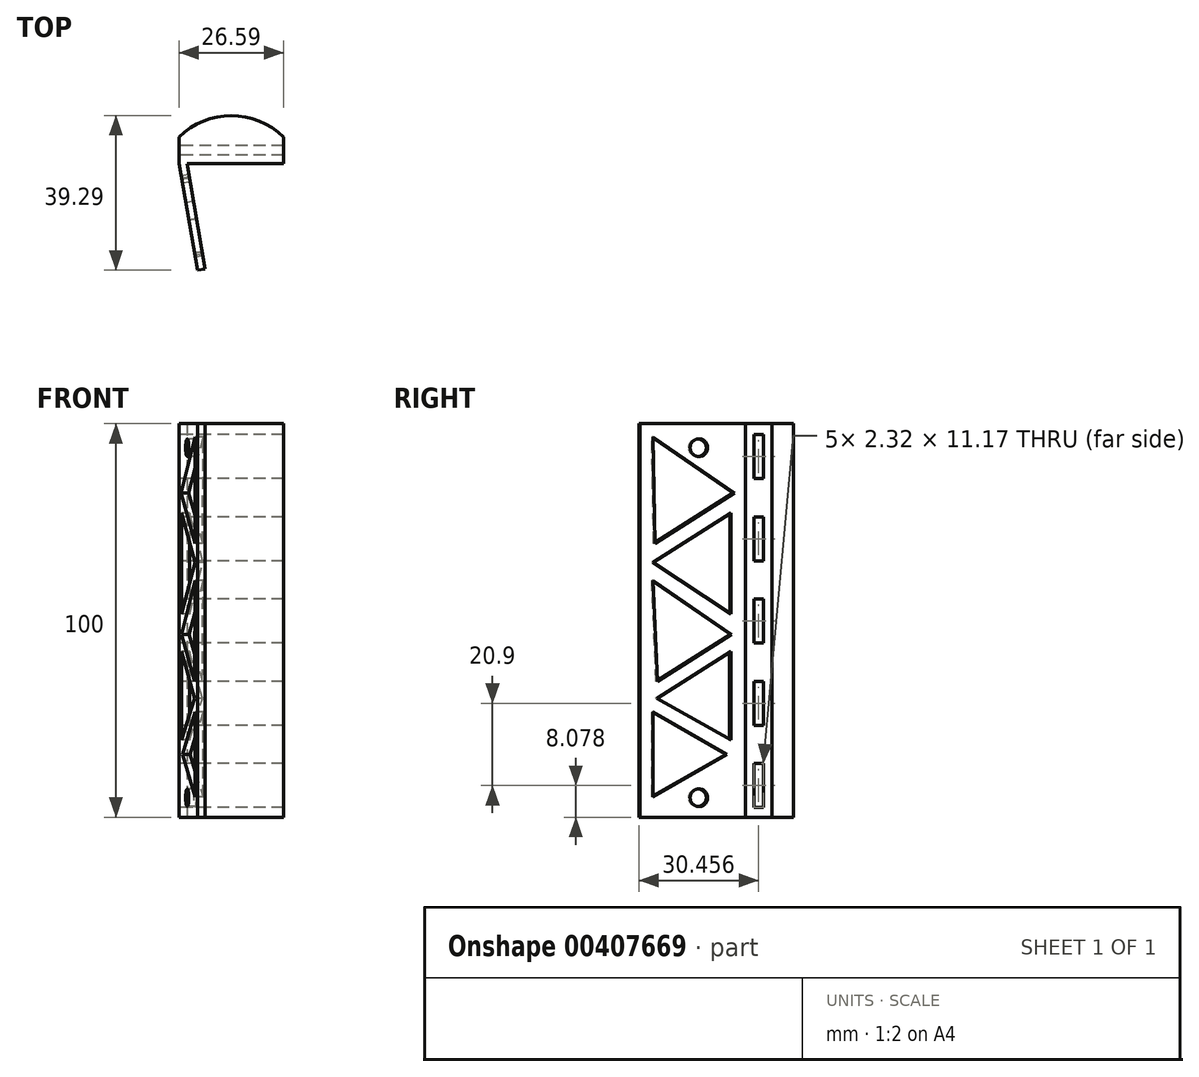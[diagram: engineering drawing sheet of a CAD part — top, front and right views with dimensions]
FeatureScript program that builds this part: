
annotation { "Feature Type Name" : "Feature", "Feature Type Description" : "" }
export const myFeature = defineFeature(function(context is Context, id is Id, definition is map)
    precondition{}
    {
        {
            var Q0;
            Q0=qCreatedBy(makeId("Top.planeOp"),FACE);
            var sketch = newSketch(context, id + "F0", { "sketchPlane" : qUnion([Q0])});
            skLineSegment(sketch, "E0.bottom", {"start": v(-13.52, 14) * mm, "end": v(13.07, 14) * mm});
            skLineSegment(sketch, "E0.top", {"start": v(-13.52, 7.33) * mm, "end": v(13.07, 7.33) * mm});
            skLineSegment(sketch, "E0.left", {"start": v(-13.52, 14) * mm, "end": v(-13.52, 7.33) * mm});
            skLineSegment(sketch, "E0.right", {"start": v(13.07, 14) * mm, "end": v(13.07, 7.33) * mm});
            skArc(sketch, "E1", {"start": v(13.07, 14) * mm, "mid": v(-0.23, 19.5) * mm, "end": v(-13.52, 14) * mm});
            skLineSegment(sketch, "E2", {"start": v(-13.52, 7.33) * mm, "end": v(-8.8, -19.79) * mm});
            skLineSegment(sketch, "E3", {"start": v(-8.8, -19.79) * mm, "end": v(-6.82, -19.44) * mm});
            skLineSegment(sketch, "E4", {"start": v(-6.82, -19.44) * mm, "end": v(-11.5, 7.33) * mm});
            skSolve(sketch);
        }
        {
            var Q0;
            Q0=makeQuery(id+"F0.imprint","IMPRINT",FACE,{"disambiguationData":[TD([[makeQuery(id+"F0.imprint","IMPRINT",EDGE,{"derivedFrom":sQuery(id+"F0.wireOp",EDGE,"E0.bottom")}),-1.0]])]});
            var Q1;
            Q1 = qSketchRegion(id + "F0", true);
            extrude(context, id + "F1", {"entities" : qUnion([Q0, Q1]), "depth" : 100 * mm, "offsetDistance" : 25 * mm});
        }
        {
            var Q0;
            Q0=makeQuery(id+"F1.opExtrude","SWEPT_FACE",FACE,{"disambiguationData":[OSD([sQuery(id+"F0.wireOp",EDGE,"E0.left")])]});
            var sketch = newSketch(context, id + "F2", { "sketchPlane" : qUnion([Q0])});
            skLineSegment(sketch, "E5.bottom", {"start": v(-11.83, 97.26) * mm, "end": v(-9.5, 97.26) * mm});
            skLineSegment(sketch, "E5.top", {"start": v(-11.83, 86.1) * mm, "end": v(-9.5, 86.1) * mm});
            skLineSegment(sketch, "E5.left", {"start": v(-11.83, 97.26) * mm, "end": v(-11.83, 86.1) * mm});
            skLineSegment(sketch, "E5.right", {"start": v(-9.5, 97.26) * mm, "end": v(-9.5, 86.1) * mm});
            skLineSegment(sketch, "E6.0.1.0", {"start": v(-9.5, 76.36) * mm, "end": v(-9.5, 65.2) * mm});
            skLineSegment(sketch, "E6.0.1.1", {"start": v(-11.83, 76.36) * mm, "end": v(-11.83, 65.2) * mm});
            skLineSegment(sketch, "E6.0.1.2", {"start": v(-11.83, 65.2) * mm, "end": v(-9.5, 65.2) * mm});
            skLineSegment(sketch, "E6.0.1.3", {"start": v(-11.83, 76.36) * mm, "end": v(-9.5, 76.36) * mm});
            skLineSegment(sketch, "E6.0.2.0", {"start": v(-9.5, 55.46) * mm, "end": v(-9.5, 44.3) * mm});
            skLineSegment(sketch, "E6.0.2.1", {"start": v(-11.83, 55.46) * mm, "end": v(-11.83, 44.3) * mm});
            skLineSegment(sketch, "E6.0.2.2", {"start": v(-11.83, 44.3) * mm, "end": v(-9.5, 44.3) * mm});
            skLineSegment(sketch, "E6.0.2.3", {"start": v(-11.83, 55.46) * mm, "end": v(-9.5, 55.46) * mm});
            skLineSegment(sketch, "E6.0.3.0", {"start": v(-9.5, 34.56) * mm, "end": v(-9.5, 23.4) * mm});
            skLineSegment(sketch, "E6.0.3.1", {"start": v(-11.83, 34.56) * mm, "end": v(-11.83, 23.4) * mm});
            skLineSegment(sketch, "E6.0.3.2", {"start": v(-11.83, 23.4) * mm, "end": v(-9.5, 23.4) * mm});
            skLineSegment(sketch, "E6.0.3.3", {"start": v(-11.83, 34.56) * mm, "end": v(-9.5, 34.56) * mm});
            skLineSegment(sketch, "E6.0.4.0", {"start": v(-9.5, 13.66) * mm, "end": v(-9.5, 2.5) * mm});
            skLineSegment(sketch, "E6.0.4.1", {"start": v(-11.83, 13.66) * mm, "end": v(-11.83, 2.5) * mm});
            skLineSegment(sketch, "E6.0.4.2", {"start": v(-11.83, 2.5) * mm, "end": v(-9.5, 2.5) * mm});
            skLineSegment(sketch, "E6.0.4.3", {"start": v(-11.83, 13.66) * mm, "end": v(-9.5, 13.66) * mm});
            skLineSegment(sketch, "E6.direction2", {"start": v(-11.83, 86.1) * mm, "end": v(-11.83, 65.2) * mm, "construction": true});
            skSolve(sketch);
        }
        {
            var Q0;
            Q0 = qSketchRegion(id + "F2", true);
            extrude(context, id + "F3", {"entities" : qUnion([Q0]), "operationType" : NewBodyOperationType.REMOVE, "endBound" : BoundingType.THROUGH_ALL, "oppositeDirection" : true, "depth" : 25 * mm, "offsetDistance" : 25 * mm});
        }
        {
            var Q0;
            Q0=makeQuery(id+"F1.opExtrude","SWEPT_FACE",FACE,{"disambiguationData":[OSD([sQuery(id+"F0.wireOp",EDGE,"E2")])]});
            var sketch = newSketch(context, id + "F4", { "sketchPlane" : qUnion([Q0])});
            skCircle(sketch, "E7", {"center": v(2.83, 93.91) * mm, "radius": 2.25 * mm});
            skCircle(sketch, "E8", {"center": v(2.83, 4.98) * mm, "radius": 2.25 * mm});
            skLineSegment(sketch, "E9", {"start": v(14.63, 96.6) * mm, "end": v(-6.33, 82.4) * mm});
            skLineSegment(sketch, "E10", {"start": v(-6.33, 82.4) * mm, "end": v(14.17, 69.6) * mm});
            skLineSegment(sketch, "E11", {"start": v(14.17, 69.6) * mm, "end": v(14.63, 96.6) * mm});
            skLineSegment(sketch, "E12", {"start": v(14.63, 64.74) * mm, "end": v(-5.5, 77.32) * mm});
            skLineSegment(sketch, "E13", {"start": v(-5.5, 77.32) * mm, "end": v(-5.5, 51.68) * mm});
            skLineSegment(sketch, "E14", {"start": v(-5.5, 51.68) * mm, "end": v(14.63, 64.74) * mm});
            skLineSegment(sketch, "E15", {"start": v(14.63, 60.21) * mm, "end": v(-5.63, 46.5) * mm});
            skLineSegment(sketch, "E16", {"start": v(-5.63, 46.5) * mm, "end": v(13.52, 34.53) * mm});
            skLineSegment(sketch, "E17", {"start": v(13.52, 34.53) * mm, "end": v(14.63, 60.21) * mm});
            skLineSegment(sketch, "E18", {"start": v(13.64, 30.22) * mm, "end": v(-5.4, 42.11) * mm});
            skLineSegment(sketch, "E19", {"start": v(-5.4, 42.11) * mm, "end": v(-5.4, 19.7) * mm});
            skLineSegment(sketch, "E20", {"start": v(-5.4, 19.7) * mm, "end": v(13.64, 30.22) * mm});
            skLineSegment(sketch, "E21", {"start": v(14.63, 26.8) * mm, "end": v(-4.45, 15.95) * mm});
            skLineSegment(sketch, "E22", {"start": v(-4.45, 15.95) * mm, "end": v(14.63, 5.23) * mm});
            skLineSegment(sketch, "E23", {"start": v(14.63, 5.23) * mm, "end": v(14.63, 26.8) * mm});
            skSolve(sketch);
        }
        {
            var Q0;
            Q0 = qSketchRegion(id + "F4", true);
            extrude(context, id + "F5", {"entities" : qUnion([Q0]), "operationType" : NewBodyOperationType.REMOVE, "oppositeDirection" : true, "depth" : 5 * mm, "offsetDistance" : 25 * mm});
        }
    });
